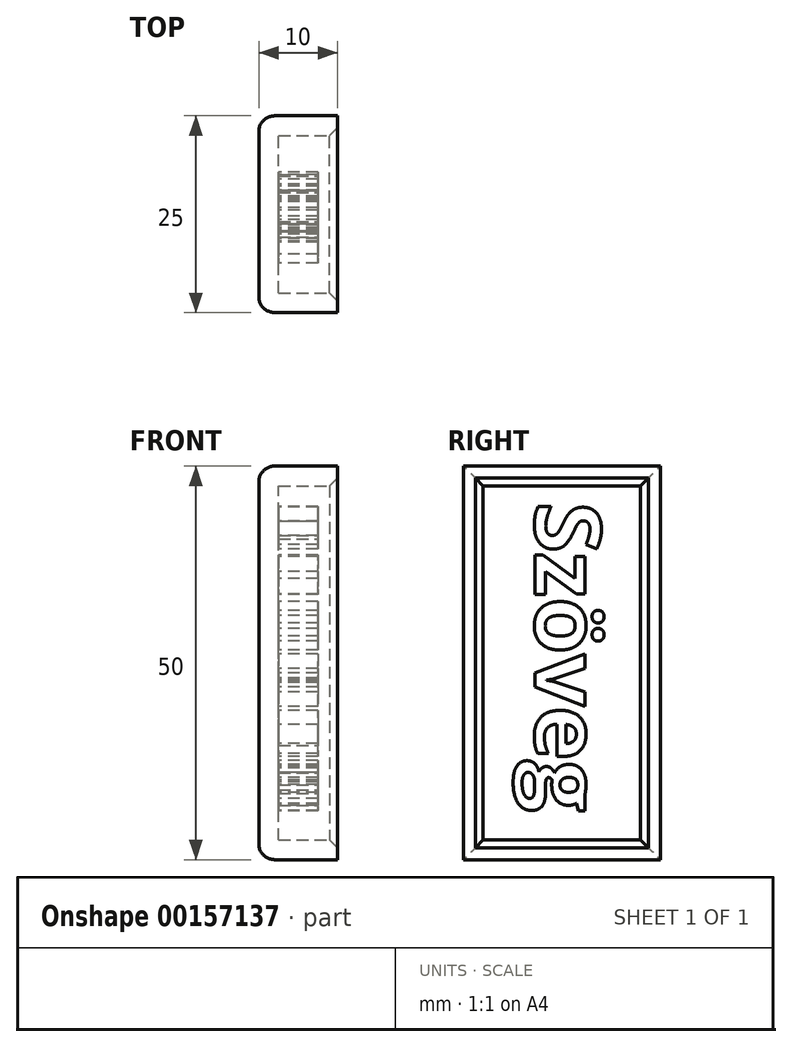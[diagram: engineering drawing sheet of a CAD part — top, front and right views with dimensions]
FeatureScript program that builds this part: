
annotation { "Feature Type Name" : "Feature", "Feature Type Description" : "" }
export const myFeature = defineFeature(function(context is Context, id is Id, definition is map)
    precondition{}
    {
        {
            var Q0;
            Q0=qCreatedBy(makeId("Front.planeOp"),FACE);
            var sketch = newSketch(context, id + "F0", { "sketchPlane" : qUnion([Q0])});
            skLineSegment(sketch, "E0.bottom", {"start": v(15.39, 1.32) * mm, "end": v(25.39, 1.32) * mm});
            skLineSegment(sketch, "E0.top", {"start": v(15.39, 51.32) * mm, "end": v(25.39, 51.32) * mm});
            skLineSegment(sketch, "E0.left", {"start": v(15.39, 1.32) * mm, "end": v(15.39, 51.32) * mm});
            skLineSegment(sketch, "E0.right", {"start": v(25.39, 1.32) * mm, "end": v(25.39, 51.32) * mm});
            skSolve(sketch);
        }
        {
            var Q0;
            Q0 = qSketchRegion(id + "F0", true);
            var Q1;
            Q1=sQuery(id+"F0.wireOp",EDGE,"E0.right");
            var Q2;
            Q2=sQuery(id+"F0.wireOp",EDGE,"E0.bottom");
            extrude(context, id + "F1", {"entities" : qUnion([Q0]), "surfaceEntities" : qUnion([Q1, Q2]), "depth" : 25 * mm});
        }
        {
            var Q0;
            Q0=makeQuery(id+"F1.opExtrude","SWEPT_FACE",FACE,{"disambiguationData":[OSD([sQuery(id+"F0.wireOp",EDGE,"E0.right")])]});
            shell(context, id + "F2", {"entities" : qUnion([Q0]), "thickness" : 2.5 * mm});
        }
        {
            var Q0;
            Q0=makeQuery(id+"F1.opExtrude","CAP_EDGE",EDGE,{"disambiguationData":[OSD([sQuery(id+"F0.wireOp",EDGE,"E0.left")])],"isStart":true});
            var Q1;
            Q1=makeQuery(id+"F1.opExtrude","SWEPT_EDGE",EDGE,{"disambiguationData":[OSD([sQuery(id+"F0.wireOp",EDGE,"E0.bottom"),sQuery(id+"F0.wireOp",EDGE,"E0.left")])]});
            var Q2;
            Q2=makeQuery(id+"F1.opExtrude","CAP_EDGE",EDGE,{"disambiguationData":[OSD([sQuery(id+"F0.wireOp",EDGE,"E0.left")])],"isStart":false});
            var Q3;
            Q3=makeQuery(id+"F1.opExtrude","SWEPT_EDGE",EDGE,{"disambiguationData":[OSD([sQuery(id+"F0.wireOp",EDGE,"E0.top"),sQuery(id+"F0.wireOp",EDGE,"E0.left")])]});
            fillet(context, id + "F3", {"entities" : qUnion([Q0, Q1, Q2, Q3]), "radius" : 2 * mm, "tangentPropagation" : true, "allowEdgeOverflow" : false});
        }
        {
            var Q0;
            {var subQ0=sQuery(id+"F0.wireOp",EDGE,"E0.right");Q0=makeQuery(id+"F2.opShell","OFFSET_EDGE",EDGE,{"disambiguationData":[OSD([subQ0]),TDD([makeQuery(id+"F1.opExtrude","CAP_EDGE",EDGE,{"disambiguationData":[OSD([subQ0])],"isStart":true})])]});}
            var Q1;
            Q1=makeQuery(id+"F2.opShell","OFFSET_EDGE",EDGE,{"disambiguationData":[OSD([sQuery(id+"F0.wireOp",EDGE,"E0.top"),sQuery(id+"F0.wireOp",EDGE,"E0.right")])]});
            var Q2;
            {var subQ0=sQuery(id+"F0.wireOp",EDGE,"E0.right");Q2=makeQuery(id+"F2.opShell","OFFSET_EDGE",EDGE,{"disambiguationData":[OSD([subQ0]),TDD([makeQuery(id+"F1.opExtrude","CAP_EDGE",EDGE,{"disambiguationData":[OSD([subQ0])],"isStart":false})])]});}
            var Q3;
            Q3=makeQuery(id+"F2.opShell","OFFSET_EDGE",EDGE,{"disambiguationData":[OSD([sQuery(id+"F0.wireOp",EDGE,"E0.bottom"),sQuery(id+"F0.wireOp",EDGE,"E0.right")])]});
            chamfer(context, id + "F4", {"entities" : qUnion([Q0, Q1, Q2, Q3]), "width" : 1 * mm, "tangentPropagation" : true});
        }
        {
            var Q0;
            Q0=makeQuery(id+"F2.opShell","OFFSET_FACE",FACE,{"disambiguationData":[OSD([sQuery(id+"F0.wireOp",EDGE,"E0.left")])]});
            var sketch = newSketch(context, id + "F5", { "sketchPlane" : qUnion([Q0])});
            skText(sketch, "E1", { "text": "Szöveg", "fontName": "OpenSans-Bold.ttf"});
            const initialGuessF5  = {"E1": [-0.0159, 0.04673, 0, -1, 0.00838]};
            skSetInitialGuess(sketch, initialGuessF5);
            skSolve(sketch);
        }
        {
            var Q0;
            Q0 = qSketchRegion(id + "F5", true);
            extrude(context, id + "F6", {"entities" : qUnion([Q0]), "operationType" : NewBodyOperationType.ADD, "depth" : 5 * mm});
        }
    });
